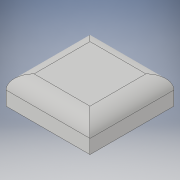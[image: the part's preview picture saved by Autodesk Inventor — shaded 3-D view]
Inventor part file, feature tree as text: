
AUTODESK INVENTOR PART (.ipt)
format: ipt  version: 2019 (Build 230136000, 136)  size: 99,840 bytes
history: native  units: mm
features: extrude x1, fillet x1, sketch x1
ambient origin geometry x8: Origin, YZ Plane, XZ Plane, XY Plane, X Axis, Y Axis, Z Axis, Center Point
bodies: Solid1 (feature_tree)
feature tree (3):
  extrude  "Extrusion1"  Depth=30.0mm
  fillet  "Fillet1"  Radius=10.0mm
  sketch  "Sketch1"  dims[d0=30.0mm d1=30.0mm d2=10.0mm d3=0.0mm d4=5.0mm]
